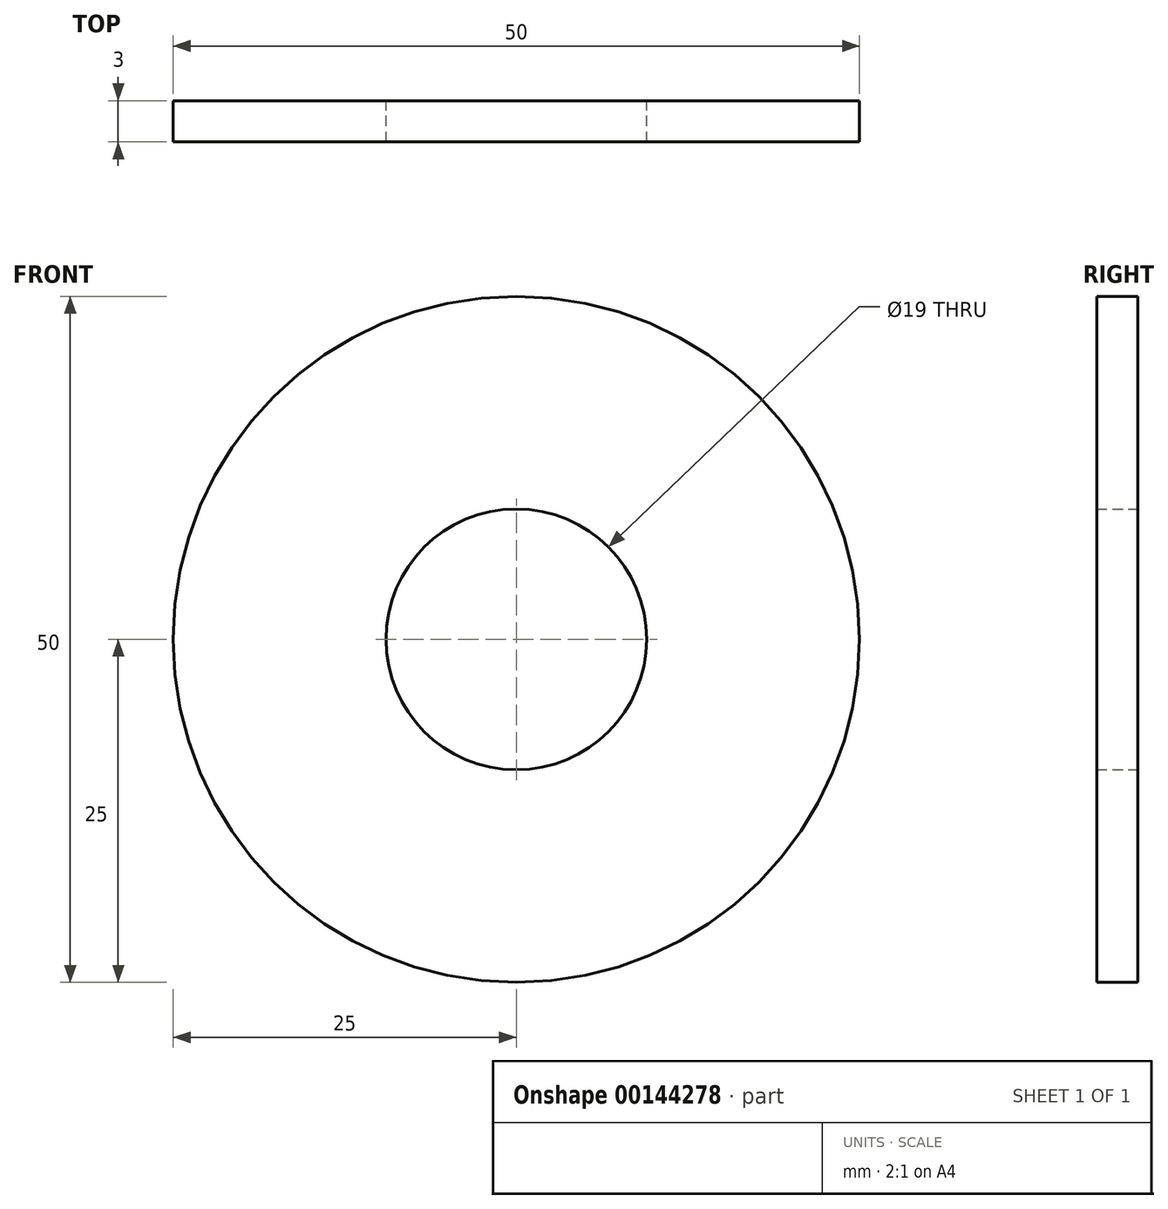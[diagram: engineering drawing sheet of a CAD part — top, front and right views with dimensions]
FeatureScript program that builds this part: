
annotation { "Feature Type Name" : "Feature", "Feature Type Description" : "" }
export const myFeature = defineFeature(function(context is Context, id is Id, definition is map)
    precondition{}
    {
        {
            var Q0;
            Q0=qCreatedBy(makeId("Front.planeOp"),FACE);
            var sketch = newSketch(context, id + "F0", { "sketchPlane" : qUnion([Q0])});
            skCircle(sketch, "E0", {"center": v(0, 0) * mm, "radius": 25 * mm});
            skLineSegment(sketch, "E1", {"start": v(0, 25) * mm, "end": v(0, -25) * mm, "construction": true});
            skCircle(sketch, "E2", {"center": v(0, 0) * mm, "radius": 9.5 * mm});
            skSolve(sketch);
        }
        {
            var Q0;
            Q0=makeQuery(id+"F0.imprint","IMPRINT",FACE,{"disambiguationData":[TD([[makeQuery(id+"F0.imprint","IMPRINT",EDGE,{"derivedFrom":sQuery(id+"F0.wireOp",EDGE,"E0")}),1.0]])]});
            extrude(context, id + "F1", {"entities" : qUnion([Q0]), "depth" : 3 * mm});
        }
    });
